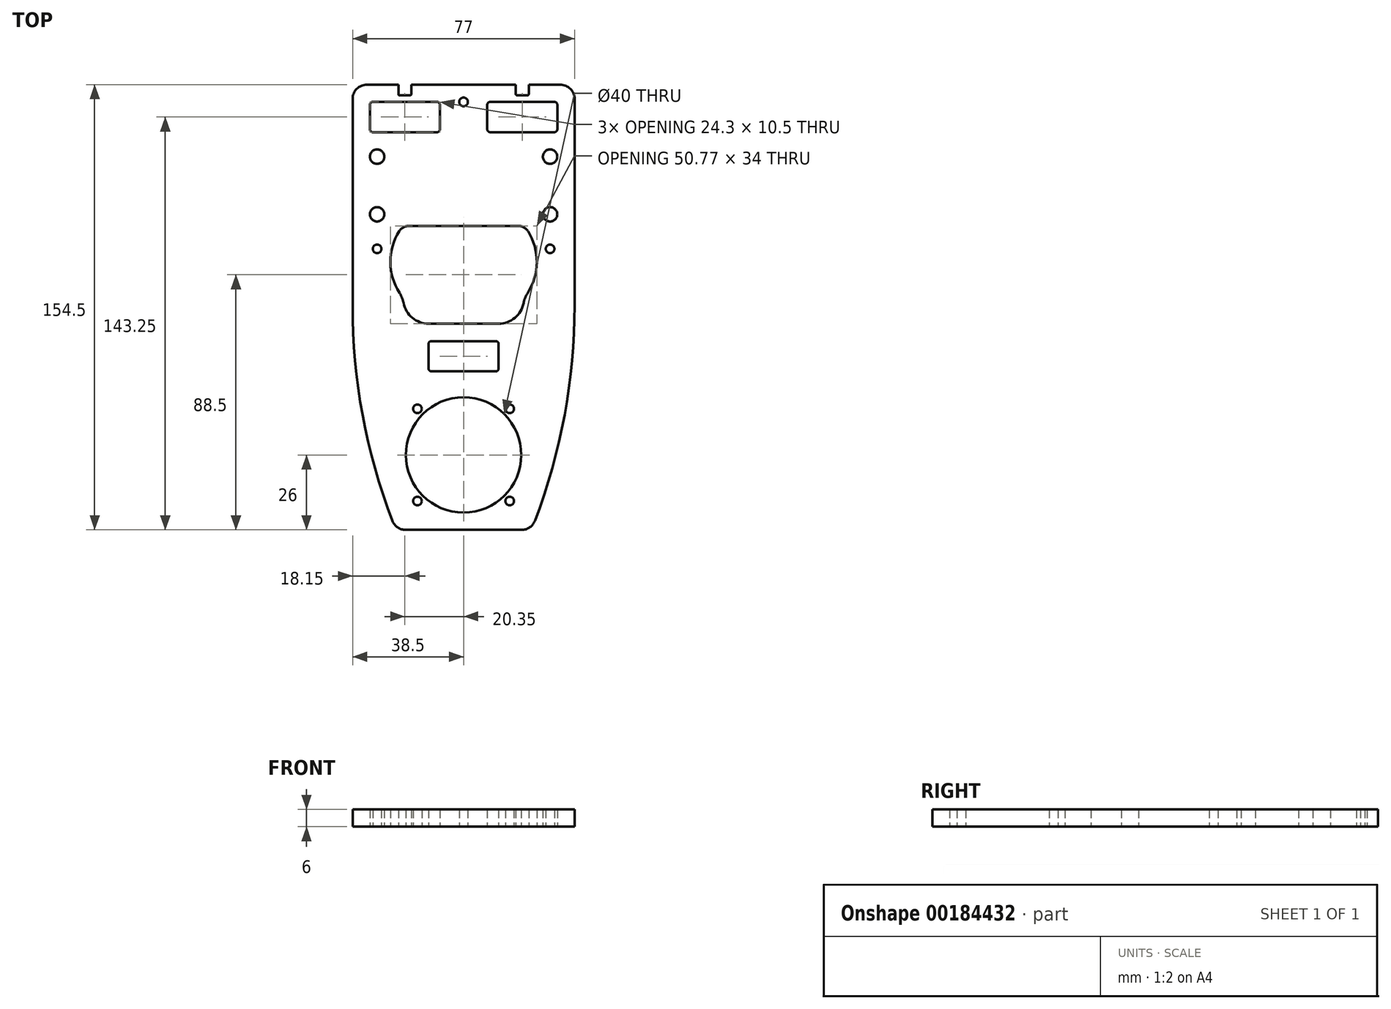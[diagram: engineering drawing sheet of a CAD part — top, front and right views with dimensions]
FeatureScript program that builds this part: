
annotation { "Feature Type Name" : "Feature", "Feature Type Description" : "" }
export const myFeature = defineFeature(function(context is Context, id is Id, definition is map)
    precondition{}
    {
        {
            var Q0;
            Q0=qCreatedBy(makeId("Top.planeOp"),FACE);
            var sketch = newSketch(context, id + "F0", { "sketchPlane" : qUnion([Q0]), "disableImprinting" : false});
            skLineSegment(sketch, "E0", {"start": v(0, 41.5) * mm, "end": v(0, -41.5) * mm, "construction": true});
            skLineSegment(sketch, "E1", {"start": v(-38.5, 41.5) * mm, "end": v(38.5, 41.5) * mm, "construction": true});
            skLineSegment(sketch, "E2", {"start": v(-23.5, -41.5) * mm, "end": v(23.5, -41.5) * mm, "construction": true});
            skLineSegment(sketch, "E3", {"start": v(-38.5, 41.5) * mm, "end": v(-38.5, 52.75) * mm});
            skLineSegment(sketch, "E4", {"start": v(-38.5, 52.75) * mm, "end": v(38.5, 52.75) * mm});
            skLineSegment(sketch, "E5", {"start": v(38.5, 52.75) * mm, "end": v(38.5, 41.5) * mm});
            skLineSegment(sketch, "E6", {"start": v(38.5, -24) * mm, "end": v(38.5, 41.5) * mm});
            skLineSegment(sketch, "E7", {"start": v(-38.5, 41.5) * mm, "end": v(-38.5, -24) * mm});
            skLineSegment(sketch, "E8", {"start": v(-23.5, -41.5) * mm, "end": v(-23.5, -52.75) * mm});
            skLineSegment(sketch, "E9", {"start": v(-23.5, -52.75) * mm, "end": v(23.5, -52.75) * mm, "construction": true});
            skLineSegment(sketch, "E10", {"start": v(23.5, -41.5) * mm, "end": v(23.5, -52.75) * mm});
            skArc(sketch, "E11", {"start": v(-38.5, -24) * mm, "mid": v(-32.85, -41.65) * mm, "end": v(-18, -52.75) * mm, "construction": true});
            skArc(sketch, "E12", {"start": v(18, -52.75) * mm, "mid": v(32.85, -41.65) * mm, "end": v(38.5, -24) * mm, "construction": true});
            skLineSegment(sketch, "E13", {"start": v(-23.5, -52.75) * mm, "end": v(-23.5, -101.75) * mm});
            skLineSegment(sketch, "E14", {"start": v(-23.5, -101.75) * mm, "end": v(23.5, -101.75) * mm});
            skLineSegment(sketch, "E15", {"start": v(23.5, -101.75) * mm, "end": v(23.5, -52.75) * mm});
            skArc(sketch, "E16", {"start": v(-38.5, -24) * mm, "mid": v(-34.72, -63.59) * mm, "end": v(-23.5, -101.75) * mm});
            skArc(sketch, "E17", {"start": v(23.5, -101.75) * mm, "mid": v(34.72, -63.59) * mm, "end": v(38.5, -24) * mm});
            skSolve(sketch);
        }
        {
            var Q0;
            Q0=qCreatedBy(makeId("Top.planeOp"),FACE);
            var sketch = newSketch(context, id + "F1", { "sketchPlane" : qUnion([Q0])});
            skCircle(sketch, "E18", {"center": v(-105.44, 38.23) * mm, "radius": 7.5 * mm, "construction": true});
            skCircle(sketch, "E19", {"center": v(-105.44, 38.23) * mm, "radius": 4 * mm, "construction": true});
            skLineSegment(sketch, "E20", {"start": v(-111.03, 43.23) * mm, "end": v(-99.85, 43.23) * mm, "construction": true});
            skLineSegment(sketch, "E21.bottom", {"start": v(-32.5, 46.75) * mm, "end": v(-8.2, 46.75) * mm});
            skLineSegment(sketch, "E21.top", {"start": v(-32.5, 36.25) * mm, "end": v(-8.2, 36.25) * mm});
            skLineSegment(sketch, "E21.left", {"start": v(-32.5, 46.75) * mm, "end": v(-32.5, 36.25) * mm});
            skLineSegment(sketch, "E21.right", {"start": v(-8.2, 46.75) * mm, "end": v(-8.2, 36.25) * mm});
            skPoint(sketch, "E22", {"position": v(-32.5, 41.5) * mm});
            skLineSegment(sketch, "E23.bottom", {"start": v(8.2, 46.75) * mm, "end": v(32.5, 46.75) * mm});
            skLineSegment(sketch, "E23.top", {"start": v(8.2, 36.25) * mm, "end": v(32.5, 36.25) * mm});
            skLineSegment(sketch, "E23.left", {"start": v(8.2, 46.75) * mm, "end": v(8.2, 36.25) * mm});
            skLineSegment(sketch, "E23.right", {"start": v(32.5, 46.75) * mm, "end": v(32.5, 36.25) * mm});
            skLineSegment(sketch, "E24.bottom", {"start": v(-12.15, -36.25) * mm, "end": v(12.15, -36.25) * mm});
            skLineSegment(sketch, "E24.top", {"start": v(-12.15, -46.75) * mm, "end": v(12.15, -46.75) * mm});
            skLineSegment(sketch, "E24.left", {"start": v(-12.15, -36.25) * mm, "end": v(-12.15, -46.75) * mm});
            skLineSegment(sketch, "E24.right", {"start": v(12.15, -36.25) * mm, "end": v(12.15, -46.75) * mm});
            skPoint(sketch, "E25", {"position": v(12.15, -41.5) * mm});
            skPoint(sketch, "E26", {"position": v(0, -36.25) * mm});
            skCircle(sketch, "E27", {"center": v(-30, 27.75) * mm, "radius": 2.5 * mm});
            skCircle(sketch, "E28", {"center": v(-30, 7.75) * mm, "radius": 2.5 * mm});
            skCircle(sketch, "E29", {"center": v(30, 27.75) * mm, "radius": 2.5 * mm});
            skCircle(sketch, "E30", {"center": v(30, 7.75) * mm, "radius": 2.5 * mm});
            skLineSegment(sketch, "E31", {"start": v(-30, 27.75) * mm, "end": v(30, 27.75) * mm, "construction": true});
            skLineSegment(sketch, "E32", {"start": v(30, 7.75) * mm, "end": v(30, 27.75) * mm, "construction": true});
            skLineSegment(sketch, "E33", {"start": v(-30, 7.75) * mm, "end": v(30, 7.75) * mm, "construction": true});
            skLineSegment(sketch, "E34", {"start": v(-30, 27.75) * mm, "end": v(-30, 7.75) * mm, "construction": true});
            skLineSegment(sketch, "E35", {"start": v(0, 27.75) * mm, "end": v(0, 7.75) * mm, "construction": true});
            skPoint(sketch, "E36", {"position": v(0, 17.75) * mm});
            skLineSegment(sketch, "E37", {"start": v(-12.15, -30.25) * mm, "end": v(12.15, -30.25) * mm});
            skPoint(sketch, "E38", {"position": v(0, -0.02) * mm});
            skPoint(sketch, "E39", {"position": v(0, -30.25) * mm});
            skLineSegment(sketch, "E40", {"start": v(-21, 3.75) * mm, "end": v(21, 3.75) * mm});
            skPoint(sketch, "E41", {"position": v(0, 3.75) * mm});
            skLineSegment(sketch, "E42", {"start": v(-21, 3.75) * mm, "end": v(-21, -21.25) * mm, "construction": true});
            skLineSegment(sketch, "E43", {"start": v(21, 3.75) * mm, "end": v(21, -21.25) * mm, "construction": true});
            skArc(sketch, "E44", {"start": v(-21, -21.25) * mm, "mid": v(-18.42, -27.56) * mm, "end": v(-12.15, -30.25) * mm});
            skArc(sketch, "E45", {"start": v(12.15, -30.25) * mm, "mid": v(18.42, -27.56) * mm, "end": v(21, -21.25) * mm});
            skLineSegment(sketch, "E46", {"start": v(-2.25, -34) * mm, "end": v(2.25, -34) * mm});
            skArc(sketch, "E47.0.startCap", {"start": v(-2.25, -34.75) * mm, "mid": v(-3, -34) * mm, "end": v(-2.25, -33.25) * mm});
            skArc(sketch, "E47.0.endCap", {"start": v(2.25, -33.25) * mm, "mid": v(3, -34) * mm, "end": v(2.25, -34.75) * mm});
            skLineSegment(sketch, "E47.0.left", {"start": v(-2.25, -33.25) * mm, "end": v(2.25, -33.25) * mm});
            skLineSegment(sketch, "E47.0.right", {"start": v(-2.25, -34.75) * mm, "end": v(2.25, -34.75) * mm});
            skPoint(sketch, "E48", {"position": v(0, -34) * mm});
            skPoint(sketch, "E49", {"position": v(-20.35, 41.5) * mm});
            skLineSegment(sketch, "E50", {"start": v(-22.6, 34) * mm, "end": v(-18.1, 34) * mm});
            skArc(sketch, "E51.0.startCap", {"start": v(-22.6, 33.25) * mm, "mid": v(-23.35, 34) * mm, "end": v(-22.6, 34.75) * mm});
            skArc(sketch, "E51.0.endCap", {"start": v(-18.1, 34.75) * mm, "mid": v(-17.35, 34) * mm, "end": v(-18.1, 33.25) * mm});
            skLineSegment(sketch, "E51.0.left", {"start": v(-22.6, 34.75) * mm, "end": v(-18.1, 34.75) * mm});
            skLineSegment(sketch, "E51.0.right", {"start": v(-22.6, 33.25) * mm, "end": v(-18.1, 33.25) * mm});
            skPoint(sketch, "E52", {"position": v(-20.35, 34) * mm});
            skLineSegment(sketch, "E53", {"start": v(18.1, 34) * mm, "end": v(22.6, 34) * mm});
            skArc(sketch, "E54.0.startCap", {"start": v(18.1, 33.25) * mm, "mid": v(17.35, 34) * mm, "end": v(18.1, 34.75) * mm});
            skArc(sketch, "E54.0.endCap", {"start": v(22.6, 34.75) * mm, "mid": v(23.35, 34) * mm, "end": v(22.6, 33.25) * mm});
            skLineSegment(sketch, "E54.0.left", {"start": v(18.1, 34.75) * mm, "end": v(22.6, 34.75) * mm});
            skLineSegment(sketch, "E54.0.right", {"start": v(18.1, 33.25) * mm, "end": v(22.6, 33.25) * mm});
            skLineSegment(sketch, "E55", {"start": v(20.35, 46.75) * mm, "end": v(20.35, 36.25) * mm, "construction": true});
            skPoint(sketch, "E56", {"position": v(20.35, 41.5) * mm});
            skPoint(sketch, "E57", {"position": v(20.35, 34) * mm});
            skLineSegment(sketch, "E58.bottom", {"start": v(-22.6, 52.75) * mm, "end": v(-18.1, 52.75) * mm});
            skLineSegment(sketch, "E58.top", {"start": v(-22.6, 49) * mm, "end": v(-18.1, 49) * mm});
            skLineSegment(sketch, "E58.left", {"start": v(-22.6, 52.75) * mm, "end": v(-22.6, 49) * mm});
            skLineSegment(sketch, "E58.right", {"start": v(-18.1, 52.75) * mm, "end": v(-18.1, 49) * mm});
            skLineSegment(sketch, "E59.bottom", {"start": v(18.1, 52.75) * mm, "end": v(22.6, 52.75) * mm});
            skLineSegment(sketch, "E59.top", {"start": v(18.1, 49) * mm, "end": v(22.6, 49) * mm});
            skLineSegment(sketch, "E59.left", {"start": v(18.1, 52.75) * mm, "end": v(18.1, 49) * mm});
            skLineSegment(sketch, "E59.right", {"start": v(22.6, 52.75) * mm, "end": v(22.6, 49) * mm});
            skPoint(sketch, "E60", {"position": v(-20.35, 49) * mm});
            skPoint(sketch, "E61", {"position": v(20.35, 49) * mm});
            skPoint(sketch, "E62", {"position": v(0, 46.75) * mm});
            skCircle(sketch, "E63", {"center": v(0, 46.75) * mm, "radius": 1.5 * mm});
            skPoint(sketch, "E64", {"position": v(32.5, 41.5) * mm});
            skArc(sketch, "E65", {"start": v(-21, 3.75) * mm, "mid": v(-25.39, -8.75) * mm, "end": v(-21, -21.25) * mm});
            skArc(sketch, "E66", {"start": v(21, -21.25) * mm, "mid": v(25.39, -8.75) * mm, "end": v(21, 3.75) * mm});
            skLineSegment(sketch, "E67", {"start": v(-30, 7.75) * mm, "end": v(-30, -36.28) * mm, "construction": true});
            skCircle(sketch, "E68", {"center": v(-30, -4.25) * mm, "radius": 1.5 * mm});
            skPoint(sketch, "E69", {"position": v(-30, -14.26) * mm});
            skLineSegment(sketch, "E70", {"start": v(30, 7.75) * mm, "end": v(30, -29.2) * mm, "construction": true});
            skCircle(sketch, "E71", {"center": v(30, -4.25) * mm, "radius": 1.5 * mm});
            skPoint(sketch, "E72", {"position": v(0, -46.75) * mm});
            skLineSegment(sketch, "E73", {"start": v(-2.25, -49) * mm, "end": v(2.25, -49) * mm});
            skPoint(sketch, "E74", {"position": v(0, -49) * mm});
            skArc(sketch, "E75.0.startCap", {"start": v(-2.25, -49.75) * mm, "mid": v(-3, -49) * mm, "end": v(-2.25, -48.25) * mm});
            skArc(sketch, "E75.0.endCap", {"start": v(2.25, -48.25) * mm, "mid": v(3, -49) * mm, "end": v(2.25, -49.75) * mm});
            skLineSegment(sketch, "E75.0.left", {"start": v(-2.25, -48.25) * mm, "end": v(2.25, -48.25) * mm});
            skLineSegment(sketch, "E75.0.right", {"start": v(-2.25, -49.75) * mm, "end": v(2.25, -49.75) * mm});
            skLineSegment(sketch, "E76.bottom", {"start": v(-20, -55.75) * mm, "end": v(20, -55.75) * mm, "construction": true});
            skLineSegment(sketch, "E76.top", {"start": v(-20, -95.75) * mm, "end": v(20, -95.75) * mm, "construction": true});
            skLineSegment(sketch, "E76.left", {"start": v(-20, -55.75) * mm, "end": v(-20, -95.75) * mm, "construction": true});
            skLineSegment(sketch, "E76.right", {"start": v(20, -55.75) * mm, "end": v(20, -95.75) * mm, "construction": true});
            skPoint(sketch, "E77", {"position": v(-20, -75.75) * mm});
            skPoint(sketch, "E78", {"position": v(0, -55.75) * mm});
            skCircle(sketch, "E79", {"center": v(0, -75.75) * mm, "radius": 20 * mm});
            skCircle(sketch, "E80", {"center": v(-16, -59.75) * mm, "radius": 1.5 * mm});
            skCircle(sketch, "E81", {"center": v(16, -59.75) * mm, "radius": 1.5 * mm});
            skCircle(sketch, "E82", {"center": v(16, -91.75) * mm, "radius": 1.5 * mm});
            skCircle(sketch, "E83", {"center": v(-16, -91.75) * mm, "radius": 1.5 * mm});
            skLineSegment(sketch, "E84", {"start": v(-20, -55.75) * mm, "end": v(20, -95.75) * mm, "construction": true});
            skLineSegment(sketch, "E85", {"start": v(-20, -95.75) * mm, "end": v(20, -55.75) * mm, "construction": true});
            skLineSegment(sketch, "E86", {"start": v(-16, -59.75) * mm, "end": v(-16, -91.75) * mm, "construction": true});
            skLineSegment(sketch, "E87", {"start": v(-16, -59.75) * mm, "end": v(16, -59.75) * mm, "construction": true});
            skPoint(sketch, "E88", {"position": v(0, -59.75) * mm});
            skPoint(sketch, "E89", {"position": v(-16, -75.75) * mm});
            skLineSegment(sketch, "E90", {"start": v(-16, -91.75) * mm, "end": v(16, -91.75) * mm, "construction": true});
            skLineSegment(sketch, "E91", {"start": v(16, -59.75) * mm, "end": v(16, -91.75) * mm, "construction": true});
            skPoint(sketch, "E92", {"position": v(16, -75.75) * mm});
            skPoint(sketch, "E93", {"position": v(0, -91.75) * mm});
            skSolve(sketch);
        }
        {
            var Q0;
            Q0=makeQuery(id+"F0.imprint","IMPRINT",FACE,{"disambiguationData":[TD([[makeQuery(id+"F0.imprint","IMPRINT",EDGE,{"derivedFrom":sQuery(id+"F0.wireOp",EDGE,"E3")}),-1.0]])]});
            extrude(context, id + "F2", {"entities" : qUnion([Q0]), "offsetDistance" : 25 * mm, "depth" : 6 * mm});
        }
        {
            var Q0;
            Q0=makeQuery(id+"F1.imprint","IMPRINT",FACE,{"disambiguationData":[TD([[makeQuery(id+"F1.imprint","IMPRINT",EDGE,{"derivedFrom":sQuery(id+"F1.wireOp",EDGE,"B3BRhq73-QkxP-cbLB-kXzY-sqsoFgEciWJY.bottom")}),-1.0]])]});
            var Q1;
            Q1=makeQuery(id+"F1.imprint","IMPRINT",FACE,{"disambiguationData":[TD([[makeQuery(id+"F1.imprint","IMPRINT",EDGE,{"derivedFrom":sQuery(id+"F1.wireOp",EDGE,"E24.bottom")}),-1.0]])]});
            var Q2;
            Q2=makeQuery(id+"F1.imprint","IMPRINT",FACE,{"disambiguationData":[TD([[makeQuery(id+"F1.imprint","IMPRINT",EDGE,{"derivedFrom":sQuery(id+"F1.wireOp",EDGE,"E47.0.startCap")}),-1.0]])]});
            var Q3;
            Q3=makeQuery(id+"F1.imprint","IMPRINT",FACE,{"disambiguationData":[TD([[makeQuery(id+"F1.imprint","IMPRINT",EDGE,{"derivedFrom":sQuery(id+"F1.wireOp",EDGE,"E37")}),1.0]])]});
            var Q4;
            Q4=makeQuery(id+"F1.imprint","IMPRINT",FACE,{"disambiguationData":[TD([[makeQuery(id+"F1.imprint","IMPRINT",EDGE,{"derivedFrom":sQuery(id+"F1.wireOp",EDGE,"E28")}),1.0]])]});
            var Q5;
            Q5=makeQuery(id+"F1.imprint","IMPRINT",FACE,{"disambiguationData":[TD([[makeQuery(id+"F1.imprint","IMPRINT",EDGE,{"derivedFrom":sQuery(id+"F1.wireOp",EDGE,"E27")}),1.0]])]});
            var Q6;
            Q6=makeQuery(id+"F1.imprint","IMPRINT",FACE,{"disambiguationData":[TD([[makeQuery(id+"F1.imprint","IMPRINT",EDGE,{"derivedFrom":sQuery(id+"F1.wireOp",EDGE,"E30")}),1.0]])]});
            var Q7;
            Q7=makeQuery(id+"F1.imprint","IMPRINT",FACE,{"disambiguationData":[TD([[makeQuery(id+"F1.imprint","IMPRINT",EDGE,{"derivedFrom":sQuery(id+"F1.wireOp",EDGE,"E29")}),1.0]])]});
            var Q8;
            Q8=makeQuery(id+"F1.imprint","IMPRINT",FACE,{"disambiguationData":[TD([[makeQuery(id+"F1.imprint","IMPRINT",EDGE,{"derivedFrom":sQuery(id+"F1.wireOp",EDGE,"E23.bottom")}),-1.0]])]});
            var Q9;
            Q9=makeQuery(id+"F1.imprint","IMPRINT",FACE,{"disambiguationData":[TD([[makeQuery(id+"F1.imprint","IMPRINT",EDGE,{"derivedFrom":sQuery(id+"F1.wireOp",EDGE,"E54.0.startCap")}),-1.0]])]});
            var Q10;
            Q10=makeQuery(id+"F1.imprint","IMPRINT",FACE,{"disambiguationData":[TD([[makeQuery(id+"F1.imprint","IMPRINT",EDGE,{"derivedFrom":sQuery(id+"F1.wireOp",EDGE,"E51.0.startCap")}),-1.0]])]});
            var Q11;
            Q11=makeQuery(id+"F1.imprint","IMPRINT",FACE,{"disambiguationData":[TD([[makeQuery(id+"F1.imprint","IMPRINT",EDGE,{"derivedFrom":sQuery(id+"F1.wireOp",EDGE,"E21.bottom")}),-1.0]])]});
            var Q12;
            Q12=makeQuery(id+"F1.imprint","IMPRINT",FACE,{"disambiguationData":[TD([[makeQuery(id+"F1.imprint","IMPRINT",EDGE,{"derivedFrom":sQuery(id+"F1.wireOp",EDGE,"E58.bottom")}),-1.0]])]});
            var Q13;
            Q13=makeQuery(id+"F1.imprint","IMPRINT",FACE,{"disambiguationData":[TD([[makeQuery(id+"F1.imprint","IMPRINT",EDGE,{"derivedFrom":sQuery(id+"F1.wireOp",EDGE,"E59.bottom")}),-1.0]])]});
            var Q14;
            Q14=makeQuery(id+"F1.imprint","IMPRINT",FACE,{"disambiguationData":[TD([[makeQuery(id+"F1.imprint","IMPRINT",EDGE,{"derivedFrom":sQuery(id+"F1.wireOp",EDGE,"E63")}),1.0]])]});
            var Q15;
            Q15=makeQuery(id+"F1.imprint","IMPRINT",FACE,{"disambiguationData":[TD([[makeQuery(id+"F1.imprint","IMPRINT",EDGE,{"derivedFrom":sQuery(id+"F1.wireOp",EDGE,"Gbfbyz53-bTuI-QxTg-yZWw-ihs9RCdUDebo")}),1.0]])]});
            var Q16;
            Q16=makeQuery(id+"F1.imprint","IMPRINT",FACE,{"disambiguationData":[TD([[makeQuery(id+"F1.imprint","IMPRINT",EDGE,{"derivedFrom":sQuery(id+"F1.wireOp",EDGE,"nBf9uIhu-Yil1-zBQY-OKYd-DtRwbnvJHZCx")}),1.0]])]});
            var Q17;
            Q17=makeQuery(id+"F1.imprint","IMPRINT",FACE,{"disambiguationData":[TD([[makeQuery(id+"F1.imprint","IMPRINT",EDGE,{"derivedFrom":sQuery(id+"F1.wireOp",EDGE,"YdwJEzvY-vDxg-1k8n-SJZq-qeKL8oMTsLEE")}),1.0]])]});
            var Q18;
            Q18=makeQuery(id+"F1.imprint","IMPRINT",FACE,{"disambiguationData":[TD([[makeQuery(id+"F1.imprint","IMPRINT",EDGE,{"derivedFrom":sQuery(id+"F1.wireOp",EDGE,"E71")}),1.0]])]});
            var Q19;
            Q19=makeQuery(id+"F1.imprint","IMPRINT",FACE,{"disambiguationData":[TD([[makeQuery(id+"F1.imprint","IMPRINT",EDGE,{"derivedFrom":sQuery(id+"F1.wireOp",EDGE,"E68")}),1.0]])]});
            var Q20;
            Q20=makeQuery(id+"F1.imprint","IMPRINT",FACE,{"disambiguationData":[TD([[makeQuery(id+"F1.imprint","IMPRINT",EDGE,{"derivedFrom":sQuery(id+"F1.wireOp",EDGE,"E79")}),1.0]])]});
            var Q21;
            Q21=makeQuery(id+"F1.imprint","IMPRINT",FACE,{"disambiguationData":[TD([[makeQuery(id+"F1.imprint","IMPRINT",EDGE,{"derivedFrom":sQuery(id+"F1.wireOp",EDGE,"E75.0.startCap")}),-1.0]])]});
            var Q22;
            Q22=makeQuery(id+"F1.imprint","IMPRINT",FACE,{"disambiguationData":[TD([[makeQuery(id+"F1.imprint","IMPRINT",EDGE,{"derivedFrom":sQuery(id+"F1.wireOp",EDGE,"E81")}),1.0]])]});
            var Q23;
            Q23=makeQuery(id+"F1.imprint","IMPRINT",FACE,{"disambiguationData":[TD([[makeQuery(id+"F1.imprint","IMPRINT",EDGE,{"derivedFrom":sQuery(id+"F1.wireOp",EDGE,"E80")}),1.0]])]});
            var Q24;
            Q24=makeQuery(id+"F1.imprint","IMPRINT",FACE,{"disambiguationData":[TD([[makeQuery(id+"F1.imprint","IMPRINT",EDGE,{"derivedFrom":sQuery(id+"F1.wireOp",EDGE,"E82")}),1.0]])]});
            var Q25;
            Q25=makeQuery(id+"F1.imprint","IMPRINT",FACE,{"disambiguationData":[TD([[makeQuery(id+"F1.imprint","IMPRINT",EDGE,{"derivedFrom":sQuery(id+"F1.wireOp",EDGE,"E83")}),1.0]])]});
            extrude(context, id + "F3", {"entities" : qUnion([Q0, Q1, Q2, Q3, Q4, Q5, Q6, Q7, Q8, Q9, Q10, Q11, Q12, Q13, Q14, Q15, Q16, Q17, Q18, Q19, Q20, Q21, Q22, Q23, Q24, Q25]), "operationType" : NewBodyOperationType.REMOVE, "endBound" : BoundingType.THROUGH_ALL, "offsetDistance" : 25 * mm, "depth" : 25 * mm});
        }
        {
            var Q0;
            Q0=makeQuery(id+"F3.boolean.opBoolean","COPY",EDGE,{"derivedFrom":makeQuery(id+"F3.opExtrude","SWEPT_EDGE",EDGE,{"disambiguationData":[OSD([sQuery(id+"F1.wireOp",EDGE,"E24.bottom"),sQuery(id+"F1.wireOp",EDGE,"E24.right")])]})});
            var Q1;
            Q1=makeQuery(id+"F3.boolean.opBoolean","COPY",EDGE,{"derivedFrom":makeQuery(id+"F3.opExtrude","SWEPT_EDGE",EDGE,{"disambiguationData":[OSD([sQuery(id+"F1.wireOp",EDGE,"E24.bottom"),sQuery(id+"F1.wireOp",EDGE,"E24.left")])]})});
            var Q2;
            Q2=makeQuery(id+"F3.boolean.opBoolean","COPY",EDGE,{"derivedFrom":makeQuery(id+"F3.opExtrude","SWEPT_EDGE",EDGE,{"disambiguationData":[OSD([sQuery(id+"F1.wireOp",EDGE,"E24.top"),sQuery(id+"F1.wireOp",EDGE,"E24.left")])]})});
            var Q3;
            Q3=makeQuery(id+"F3.boolean.opBoolean","COPY",EDGE,{"derivedFrom":makeQuery(id+"F3.opExtrude","SWEPT_EDGE",EDGE,{"disambiguationData":[OSD([sQuery(id+"F1.wireOp",EDGE,"E24.top"),sQuery(id+"F1.wireOp",EDGE,"E24.right")])]})});
            var Q4;
            Q4=makeQuery(id+"F3.boolean.opBoolean","COPY",EDGE,{"derivedFrom":makeQuery(id+"F3.opExtrude","SWEPT_EDGE",EDGE,{"disambiguationData":[OSD([sQuery(id+"F1.wireOp",EDGE,"E23.bottom"),sQuery(id+"F1.wireOp",EDGE,"E23.left")])]})});
            var Q5;
            Q5=makeQuery(id+"F3.boolean.opBoolean","COPY",EDGE,{"derivedFrom":makeQuery(id+"F3.opExtrude","SWEPT_EDGE",EDGE,{"disambiguationData":[OSD([sQuery(id+"F1.wireOp",EDGE,"E21.bottom"),sQuery(id+"F1.wireOp",EDGE,"E21.left")])]})});
            var Q6;
            Q6=makeQuery(id+"F3.boolean.opBoolean","COPY",EDGE,{"derivedFrom":makeQuery(id+"F3.opExtrude","SWEPT_EDGE",EDGE,{"disambiguationData":[OSD([sQuery(id+"F1.wireOp",EDGE,"E21.top"),sQuery(id+"F1.wireOp",EDGE,"E21.left")])]})});
            var Q7;
            Q7=makeQuery(id+"F3.boolean.opBoolean","COPY",EDGE,{"derivedFrom":makeQuery(id+"F3.opExtrude","SWEPT_EDGE",EDGE,{"disambiguationData":[OSD([sQuery(id+"F1.wireOp",EDGE,"E21.bottom"),sQuery(id+"F1.wireOp",EDGE,"E21.right")])]})});
            var Q8;
            Q8=makeQuery(id+"F3.boolean.opBoolean","COPY",EDGE,{"derivedFrom":makeQuery(id+"F3.opExtrude","SWEPT_EDGE",EDGE,{"disambiguationData":[OSD([sQuery(id+"F1.wireOp",EDGE,"E21.top"),sQuery(id+"F1.wireOp",EDGE,"E21.right")])]})});
            var Q9;
            Q9=makeQuery(id+"F3.boolean.opBoolean","COPY",EDGE,{"derivedFrom":makeQuery(id+"F3.opExtrude","SWEPT_EDGE",EDGE,{"disambiguationData":[OSD([sQuery(id+"F1.wireOp",EDGE,"E23.top"),sQuery(id+"F1.wireOp",EDGE,"E23.right")])]})});
            var Q10;
            Q10=makeQuery(id+"F3.boolean.opBoolean","COPY",EDGE,{"derivedFrom":makeQuery(id+"F3.opExtrude","SWEPT_EDGE",EDGE,{"disambiguationData":[OSD([sQuery(id+"F1.wireOp",EDGE,"E23.top"),sQuery(id+"F1.wireOp",EDGE,"E23.left")])]})});
            var Q11;
            Q11=makeQuery(id+"F3.boolean.opBoolean","COPY",EDGE,{"derivedFrom":makeQuery(id+"F3.opExtrude","SWEPT_EDGE",EDGE,{"disambiguationData":[OSD([sQuery(id+"F1.wireOp",EDGE,"E23.bottom"),sQuery(id+"F1.wireOp",EDGE,"E23.right")])]})});
            fillet(context, id + "F4", {"entities" : qUnion([Q0, Q1, Q2, Q3, Q4, Q5, Q6, Q7, Q8, Q9, Q10, Q11]), "radius" : 1 * mm, "tangentPropagation" : true, "allowEdgeOverflow" : false});
        }
        {
            var Q0;
            Q0=makeQuery(id+"F3.boolean.opBoolean","COPY",EDGE,{"derivedFrom":makeQuery(id+"F3.opExtrude","SWEPT_EDGE",EDGE,{"disambiguationData":[OSD([sQuery(id+"F1.wireOp",EDGE,"B3BRhq73-QkxP-cbLB-kXzY-sqsoFgEciWJY.bottom"),sQuery(id+"F1.wireOp",EDGE,"B3BRhq73-QkxP-cbLB-kXzY-sqsoFgEciWJY.right")])]})});
            var Q1;
            Q1=makeQuery(id+"F3.boolean.opBoolean","COPY",EDGE,{"derivedFrom":makeQuery(id+"F3.opExtrude","SWEPT_EDGE",EDGE,{"disambiguationData":[OSD([sQuery(id+"F1.wireOp",EDGE,"B3BRhq73-QkxP-cbLB-kXzY-sqsoFgEciWJY.bottom"),sQuery(id+"F1.wireOp",EDGE,"B3BRhq73-QkxP-cbLB-kXzY-sqsoFgEciWJY.left")])]})});
            var Q2;
            Q2=makeQuery(id+"F3.boolean.opBoolean","COPY",EDGE,{"derivedFrom":makeQuery(id+"F3.opExtrude","SWEPT_EDGE",EDGE,{"disambiguationData":[OSD([sQuery(id+"F1.wireOp",EDGE,"E59.top"),sQuery(id+"F1.wireOp",EDGE,"E59.left")])]})});
            var Q3;
            Q3=makeQuery(id+"F3.boolean.opBoolean","COPY",EDGE,{"derivedFrom":makeQuery(id+"F3.opExtrude","SWEPT_EDGE",EDGE,{"disambiguationData":[OSD([sQuery(id+"F1.wireOp",EDGE,"E59.top"),sQuery(id+"F1.wireOp",EDGE,"E59.right")])]})});
            var Q4;
            Q4=makeQuery(id+"F3.boolean.opBoolean","COPY",EDGE,{"derivedFrom":makeQuery(id+"F3.opExtrude","SWEPT_EDGE",EDGE,{"disambiguationData":[OSD([sQuery(id+"F1.wireOp",EDGE,"E58.top"),sQuery(id+"F1.wireOp",EDGE,"E58.right")])]})});
            var Q5;
            Q5=makeQuery(id+"F3.boolean.opBoolean","COPY",EDGE,{"derivedFrom":makeQuery(id+"F3.opExtrude","SWEPT_EDGE",EDGE,{"disambiguationData":[OSD([sQuery(id+"F1.wireOp",EDGE,"E58.top"),sQuery(id+"F1.wireOp",EDGE,"E58.left")])]})});
            var Q6;
            Q6=makeQuery(id+"F3.boolean.opBoolean","COPY",EDGE,{"derivedFrom":makeQuery(id+"F3.opExtrude","SWEPT_EDGE",EDGE,{"disambiguationData":[OSD([sQuery(id+"F1.wireOp",EDGE,"E58.bottom"),sQuery(id+"F1.wireOp",EDGE,"E58.left")])]})});
            var Q7;
            Q7=makeQuery(id+"F3.boolean.opBoolean","COPY",EDGE,{"derivedFrom":makeQuery(id+"F3.opExtrude","SWEPT_EDGE",EDGE,{"disambiguationData":[OSD([sQuery(id+"F1.wireOp",EDGE,"E58.bottom"),sQuery(id+"F1.wireOp",EDGE,"E58.right")])]})});
            var Q8;
            Q8=makeQuery(id+"F3.boolean.opBoolean","COPY",EDGE,{"derivedFrom":makeQuery(id+"F3.opExtrude","SWEPT_EDGE",EDGE,{"disambiguationData":[OSD([sQuery(id+"F1.wireOp",EDGE,"E59.bottom"),sQuery(id+"F1.wireOp",EDGE,"E59.left")])]})});
            var Q9;
            Q9=makeQuery(id+"F3.boolean.opBoolean","COPY",EDGE,{"derivedFrom":makeQuery(id+"F3.opExtrude","SWEPT_EDGE",EDGE,{"disambiguationData":[OSD([sQuery(id+"F1.wireOp",EDGE,"E59.bottom"),sQuery(id+"F1.wireOp",EDGE,"E59.right")])]})});
            var Q10;
            Q10=makeQuery(id+"F3.boolean.opBoolean","COPY",EDGE,{"derivedFrom":makeQuery(id+"F3.opExtrude","SWEPT_EDGE",EDGE,{"disambiguationData":[OSD([sQuery(id+"F1.wireOp",EDGE,"B3BRhq73-QkxP-cbLB-kXzY-sqsoFgEciWJY.top"),sQuery(id+"F1.wireOp",EDGE,"B3BRhq73-QkxP-cbLB-kXzY-sqsoFgEciWJY.left")])]})});
            var Q11;
            Q11=makeQuery(id+"F3.boolean.opBoolean","COPY",EDGE,{"derivedFrom":makeQuery(id+"F3.opExtrude","SWEPT_EDGE",EDGE,{"disambiguationData":[OSD([sQuery(id+"F1.wireOp",EDGE,"B3BRhq73-QkxP-cbLB-kXzY-sqsoFgEciWJY.top"),sQuery(id+"F1.wireOp",EDGE,"B3BRhq73-QkxP-cbLB-kXzY-sqsoFgEciWJY.right")])]})});
            fillet(context, id + "F5", {"entities" : qUnion([Q0, Q1, Q2, Q3, Q4, Q5, Q6, Q7, Q8, Q9, Q10, Q11]), "radius" : .5 * mm, "tangentPropagation" : true, "allowEdgeOverflow" : false});
        }
        {
            var Q0;
            Q0=makeQuery(id+"F3.boolean.opBoolean","COPY",EDGE,{"derivedFrom":makeQuery(id+"F3.opExtrude","SWEPT_EDGE",EDGE,{"disambiguationData":[OSD([sQuery(id+"F1.wireOp",EDGE,"E40"),sQuery(id+"F1.wireOp",EDGE,"E42")])]})});
            var Q1;
            Q1=makeQuery(id+"F3.boolean.opBoolean","COPY",EDGE,{"derivedFrom":makeQuery(id+"F3.opExtrude","SWEPT_EDGE",EDGE,{"disambiguationData":[OSD([sQuery(id+"F1.wireOp",EDGE,"E40"),sQuery(id+"F1.wireOp",EDGE,"E43")])]})});
            fillet(context, id + "F6", {"entities" : qUnion([Q0, Q1]), "radius" : 4 * mm, "tangentPropagation" : true, "allowEdgeOverflow" : false});
        }
        {
            var Q0;
            Q0=makeQuery(id+"F2.opExtrude","SWEPT_EDGE",EDGE,{"disambiguationData":[OSD([sQuery(id+"F0.wireOp",EDGE,"E9"),sQuery(id+"F0.wireOp",EDGE,"E11")])]});
            var Q1;
            Q1=makeQuery(id+"F2.opExtrude","SWEPT_EDGE",EDGE,{"disambiguationData":[OSD([sQuery(id+"F0.wireOp",EDGE,"E9"),sQuery(id+"F0.wireOp",EDGE,"E12")])]});
            var Q2;
            Q2=makeQuery(id+"F2.opExtrude","SWEPT_EDGE",EDGE,{"disambiguationData":[OSD([sQuery(id+"F0.wireOp",EDGE,"E14"),sQuery(id+"F0.wireOp",EDGE,"E16")])]});
            var Q3;
            Q3=makeQuery(id+"F2.opExtrude","SWEPT_EDGE",EDGE,{"disambiguationData":[OSD([sQuery(id+"F0.wireOp",EDGE,"E14"),sQuery(id+"F0.wireOp",EDGE,"E17")])]});
            var Q4;
            Q4=makeQuery(id+"F2.opExtrude","SWEPT_EDGE",EDGE,{"disambiguationData":[OSD([sQuery(id+"F0.wireOp",EDGE,"E3"),sQuery(id+"F0.wireOp",EDGE,"E4")])]});
            var Q5;
            Q5=makeQuery(id+"F2.opExtrude","SWEPT_EDGE",EDGE,{"disambiguationData":[OSD([sQuery(id+"F0.wireOp",EDGE,"E4"),sQuery(id+"F0.wireOp",EDGE,"E5")])]});
            fillet(context, id + "F7", {"entities" : qUnion([Q0, Q1, Q2, Q3, Q4, Q5]), "radius" : 5 * mm, "tangentPropagation" : true, "allowEdgeOverflow" : false});
        }
        {
            var Q0;
            Q0=makeQuery(id+"F3.boolean.opBoolean","COPY",EDGE,{"derivedFrom":makeQuery(id+"F3.opExtrude","SWEPT_EDGE",EDGE,{"disambiguationData":[OSD([sQuery(id+"F1.wireOp",EDGE,"E44"),sQuery(id+"F1.wireOp",EDGE,"E65")])]})});
            var Q1;
            Q1=makeQuery(id+"F3.boolean.opBoolean","COPY",EDGE,{"derivedFrom":makeQuery(id+"F3.opExtrude","SWEPT_EDGE",EDGE,{"disambiguationData":[OSD([sQuery(id+"F1.wireOp",EDGE,"E45"),sQuery(id+"F1.wireOp",EDGE,"E66")])]})});
            fillet(context, id + "F8", {"entities" : qUnion([Q0, Q1]), "radius" : 10 * mm, "tangentPropagation" : true, "allowEdgeOverflow" : false});
        }
    });
